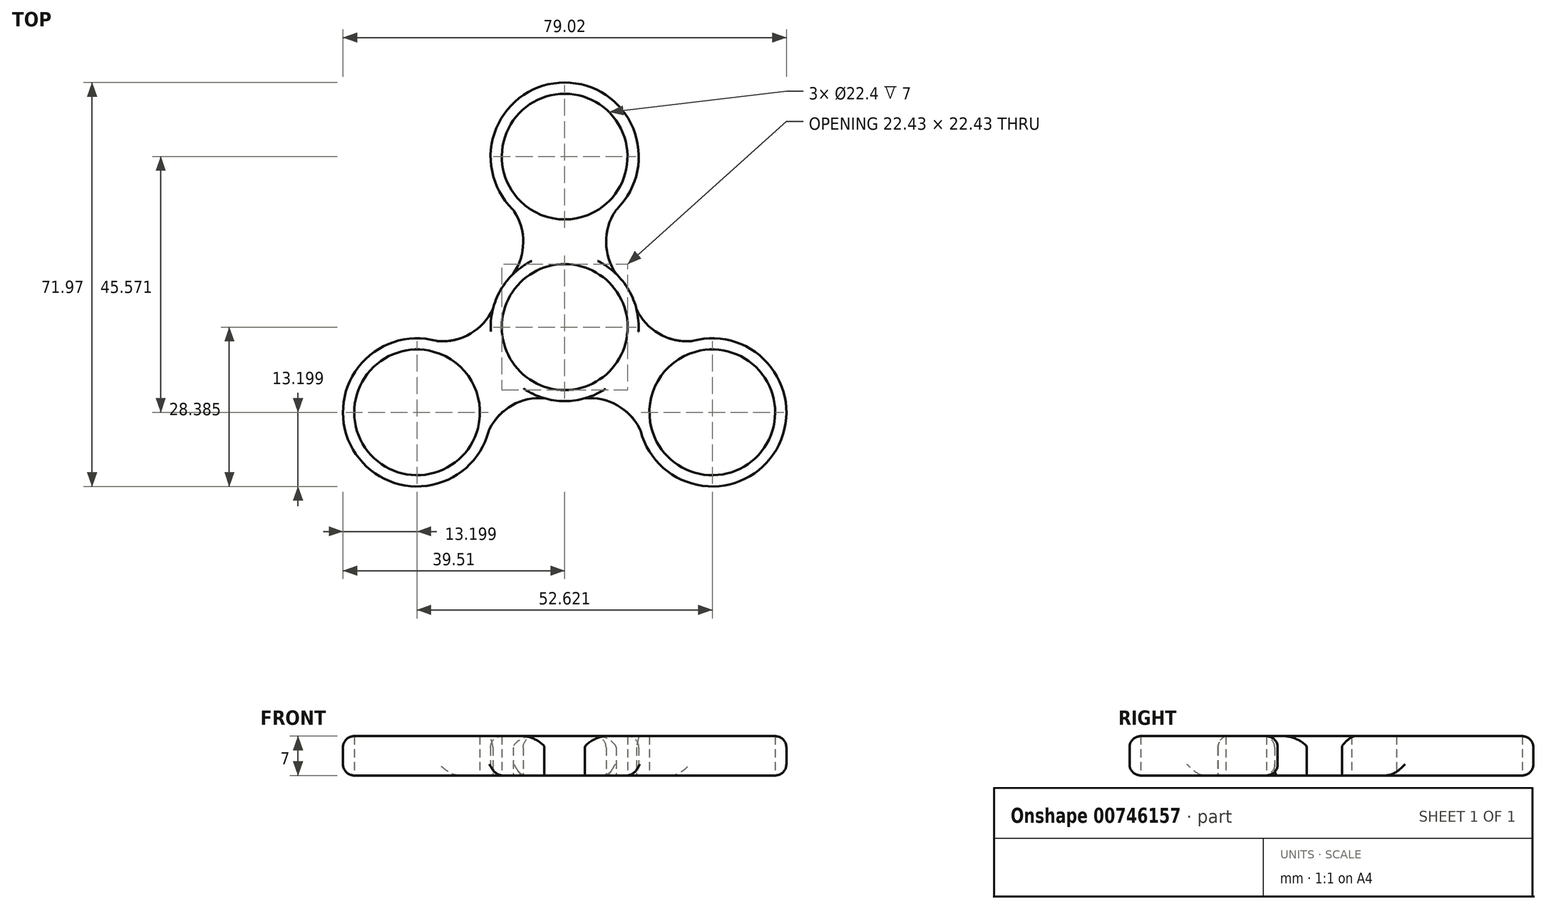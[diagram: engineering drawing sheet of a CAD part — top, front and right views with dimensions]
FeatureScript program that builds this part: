
annotation { "Feature Type Name" : "Feature", "Feature Type Description" : "" }
export const myFeature = defineFeature(function(context is Context, id is Id, definition is map)
    precondition{}
    {
        {
            var Q0;
            Q0=qCreatedBy(makeId("Top.planeOp"),FACE);
            var sketch = newSketch(context, id + "F0", { "sketchPlane" : qUnion([Q0])});
            skCircle(sketch, "E0", {"center": v(0, 0) * mm, "radius": 11.2 * mm});
            skArc(sketch, "E1", {"start": v(-9.17, 9.5) * mm, "mid": v(-11.43, 6.6) * mm, "end": v(-12.81, 3.18) * mm});
            skCircle(sketch, "E2", {"center": v(0, 30.4) * mm, "radius": 11.2 * mm});
            skArc(sketch, "E3", {"start": v(9.16, 20.9) * mm, "mid": v(0, 43.6) * mm, "end": v(-9.16, 20.9) * mm});
            skArc(sketch, "E4", {"start": v(-9.17, 9.5) * mm, "mid": v(-7.38, 15.2) * mm, "end": v(-9.16, 20.9) * mm});
            skArc(sketch, "E5", {"start": v(9.16, 20.9) * mm, "mid": v(7.38, 15.2) * mm, "end": v(9.17, 9.5) * mm});
            skCircle(sketch, "E6.1.0", {"center": v(-26.31, -15.17) * mm, "radius": 11.2 * mm});
            skArc(sketch, "E6.1.1", {"start": v(-22.66, -2.49) * mm, "mid": v(-37.74, -21.77) * mm, "end": v(-13.5, -18.35) * mm});
            skArc(sketch, "E6.1.2", {"start": v(-22.66, -2.49) * mm, "mid": v(-16.83, -1.18) * mm, "end": v(-12.8, 3.22) * mm});
            skArc(sketch, "E6.1.3", {"start": v(-3.62, -12.66) * mm, "mid": v(-9.45, -13.96) * mm, "end": v(-13.5, -18.35) * mm});
            skCircle(sketch, "E6.1.4", {"center": v(0.02, 0.03) * mm, "radius": 11.2 * mm});
            skArc(sketch, "E6.1.5", {"start": v(-3.62, -12.66) * mm, "mid": v(0.02, -13.17) * mm, "end": v(3.67, -12.66) * mm});
            skCircle(sketch, "E6.2.0", {"center": v(26.31, -15.17) * mm, "radius": 11.2 * mm});
            skArc(sketch, "E6.2.1", {"start": v(13.5, -18.35) * mm, "mid": v(37.74, -21.77) * mm, "end": v(22.66, -2.49) * mm});
            skArc(sketch, "E6.2.2", {"start": v(13.5, -18.35) * mm, "mid": v(9.45, -13.96) * mm, "end": v(3.62, -12.66) * mm});
            skArc(sketch, "E6.2.3", {"start": v(12.8, 3.22) * mm, "mid": v(16.83, -1.18) * mm, "end": v(22.66, -2.49) * mm});
            skCircle(sketch, "E6.2.4", {"center": v(-0.02, 0.03) * mm, "radius": 11.2 * mm});
            skArc(sketch, "E6.2.5", {"start": v(12.8, 3.22) * mm, "mid": v(11.41, 6.63) * mm, "end": v(9.14, 9.53) * mm});
            skPoint(sketch, "E6.center", {"position": v(0, 0.02) * mm});
            skArc(sketch, "E7.trimOffspring", {"start": v(-3.67, -12.66) * mm, "mid": v(-0.02, -13.17) * mm, "end": v(3.62, -12.66) * mm});
            skArc(sketch, "E8.trimOffspring", {"start": v(12.86, 3.08) * mm, "mid": v(11.45, 6.63) * mm, "end": v(9.08, 9.62) * mm});
            skArc(sketch, "E9.trimOffspring", {"start": v(-3.78, -12.65) * mm, "mid": v(0, -13.2) * mm, "end": v(3.78, -12.65) * mm});
            skArc(sketch, "E10.trimOffspring", {"start": v(12.81, 3.18) * mm, "mid": v(11.43, 6.6) * mm, "end": v(9.17, 9.5) * mm});
            skArc(sketch, "E11.trimOffspring", {"start": v(-9.08, 9.62) * mm, "mid": v(-11.45, 6.63) * mm, "end": v(-12.86, 3.08) * mm});
            skArc(sketch, "E12.trimOffspring", {"start": v(-9.14, 9.53) * mm, "mid": v(-11.41, 6.63) * mm, "end": v(-12.8, 3.22) * mm});
            skSolve(sketch);
        }
        {
            var Q0;
            Q0=makeQuery(id+"F0.imprint","IMPRINT",FACE,{"disambiguationData":[TD([[makeQuery(id+"F0.imprint","IMPRINT",EDGE,{"derivedFrom":sQuery(id+"F0.wireOp",EDGE,"E2")}),-1.0]])]});
            extrude(context, id + "F1", {"entities" : qUnion([Q0]), "depth" : 7 * mm, "offsetDistance" : 25 * mm});
        }
        {
            var Q0;
            Q0=makeQuery(id+"F1.opExtrude","CAP_EDGE",EDGE,{"disambiguationData":[OSD([sQuery(id+"F0.wireOp",EDGE,"E6.1.3")])],"isStart":false});
            var Q1;
            Q1=makeQuery(id+"F1.opExtrude","CAP_EDGE",EDGE,{"disambiguationData":[OSD([sQuery(id+"F0.wireOp",EDGE,"E6.2.2")])],"isStart":false});
            var Q2;
            Q2=makeQuery(id+"F1.opExtrude","CAP_EDGE",EDGE,{"disambiguationData":[OSD([sQuery(id+"F0.wireOp",EDGE,"E4")])],"isStart":false});
            var Q3;
            Q3=makeQuery(id+"F1.opExtrude","CAP_EDGE",EDGE,{"disambiguationData":[OSD([sQuery(id+"F0.wireOp",EDGE,"E6.1.2")])],"isStart":false});
            var Q4;
            Q4=makeQuery(id+"F1.opExtrude","CAP_EDGE",EDGE,{"disambiguationData":[OSD([sQuery(id+"F0.wireOp",EDGE,"E6.2.3")])],"isStart":false});
            var Q5;
            Q5=makeQuery(id+"F1.opExtrude","CAP_EDGE",EDGE,{"disambiguationData":[OSD([sQuery(id+"F0.wireOp",EDGE,"E5")])],"isStart":false});
            var Q6;
            Q6=makeQuery(id+"F1.opExtrude","SWEPT_FACE",FACE,{"disambiguationData":[OSD([sQuery(id+"F0.wireOp",EDGE,"E6.2.1")])]});
            var Q7;
            Q7=makeQuery(id+"F1.opExtrude","SWEPT_FACE",FACE,{"disambiguationData":[OSD([sQuery(id+"F0.wireOp",EDGE,"E3")])]});
            var Q8;
            Q8=makeQuery(id+"F1.opExtrude","SWEPT_FACE",FACE,{"disambiguationData":[OSD([sQuery(id+"F0.wireOp",EDGE,"E6.1.1")])]});
            fillet(context, id + "F2", {"entities" : qUnion([Q0, Q1, Q2, Q3, Q4, Q5, Q6, Q7, Q8]), "radius" : 2 * mm, "tangentPropagation" : true, "allowEdgeOverflow" : false});
        }
    });
